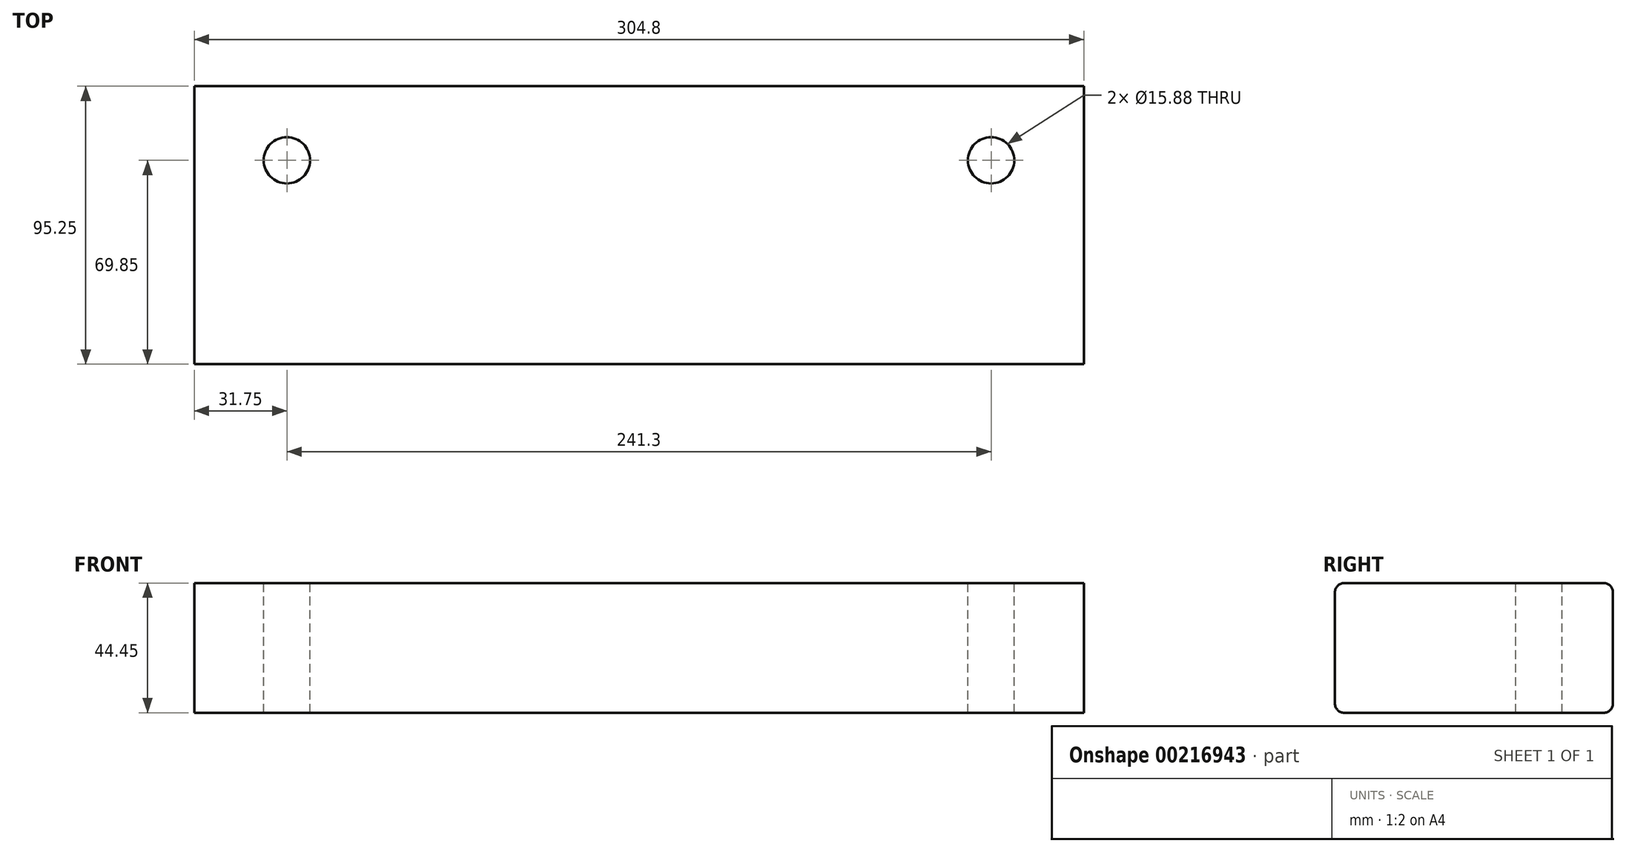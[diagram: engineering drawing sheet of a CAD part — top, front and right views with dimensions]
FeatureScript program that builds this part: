
annotation { "Feature Type Name" : "Feature", "Feature Type Description" : "" }
export const myFeature = defineFeature(function(context is Context, id is Id, definition is map)
    precondition{}
    {
        {
            var Q0;
            Q0=qCreatedBy(makeId("Top.planeOp"),FACE);
            var sketch = newSketch(context, id + "F0", { "sketchPlane" : qUnion([Q0])});
            skLineSegment(sketch, "E0.bottom", {"start": v(0, 0) * mm, "end": v(304.8, 0) * mm});
            skLineSegment(sketch, "E0.top", {"start": v(0, 95.25) * mm, "end": v(304.8, 95.25) * mm});
            skLineSegment(sketch, "E0.left", {"start": v(0, 0) * mm, "end": v(0, 95.25) * mm});
            skLineSegment(sketch, "E0.right", {"start": v(304.8, 0) * mm, "end": v(304.8, 95.25) * mm});
            skSolve(sketch);
        }
        {
            var Q0;
            Q0 = qSketchRegion(id + "F0", true);
            extrude(context, id + "F1", {"entities" : qUnion([Q0]), "depth" : 44.45 * mm});
        }
        {
            var Q0;
            Q0=makeQuery(id+"F1.opExtrude","CAP_EDGE",EDGE,{"disambiguationData":[OSD([sQuery(id+"F0.wireOp",EDGE,"E0.top")])],"isStart":false});
            var Q1;
            Q1=makeQuery(id+"F1.opExtrude","CAP_EDGE",EDGE,{"disambiguationData":[OSD([sQuery(id+"F0.wireOp",EDGE,"E0.bottom")])],"isStart":false});
            var Q2;
            Q2=makeQuery(id+"F1.opExtrude","CAP_EDGE",EDGE,{"disambiguationData":[OSD([sQuery(id+"F0.wireOp",EDGE,"E0.bottom")])],"isStart":true});
            var Q3;
            Q3=makeQuery(id+"F1.opExtrude","CAP_EDGE",EDGE,{"disambiguationData":[OSD([sQuery(id+"F0.wireOp",EDGE,"E0.top")])],"isStart":true});
            fillet(context, id + "F2", {"entities" : qUnion([Q0, Q1, Q2, Q3]), "radius" : 3.17 * mm, "tangentPropagation" : true, "allowEdgeOverflow" : false});
        }
        {
            var Q0;
            Q0=makeQuery(id+"F1.opExtrude","CAP_FACE",FACE,{"disambiguationData":[OSD([sQuery(id+"F0.wireOp",EDGE,"E0.bottom"),sQuery(id+"F0.wireOp",EDGE,"E0.top"),sQuery(id+"F0.wireOp",EDGE,"E0.left"),sQuery(id+"F0.wireOp",EDGE,"E0.right")])],"isStart":false});
            var sketch = newSketch(context, id + "F3", { "sketchPlane" : qUnion([Q0])});
            skLineSegment(sketch, "E1", {"start": v(152.4, 92.08) * mm, "end": v(152.4, 3.17) * mm, "construction": true});
            skCircle(sketch, "E2", {"center": v(31.75, 69.85) * mm, "radius": 7.94 * mm});
            skLineSegment(sketch, "E3", {"start": v(0, 69.85) * mm, "end": v(31.75, 69.85) * mm, "construction": true});
            skLineSegment(sketch, "E4", {"start": v(31.75, 69.85) * mm, "end": v(31.75, 95.25) * mm, "construction": true});
            skCircle(sketch, "E5.MirrorC", {"center": v(273.05, 69.85) * mm, "radius": 7.94 * mm});
            skSolve(sketch);
        }
        {
            var Q0;
            Q0 = qSketchRegion(id + "F3", true);
            extrude(context, id + "F4", {"entities" : qUnion([Q0]), "operationType" : NewBodyOperationType.REMOVE, "endBound" : BoundingType.THROUGH_ALL, "oppositeDirection" : true, "depth" : 25.4 * mm});
        }
    });
